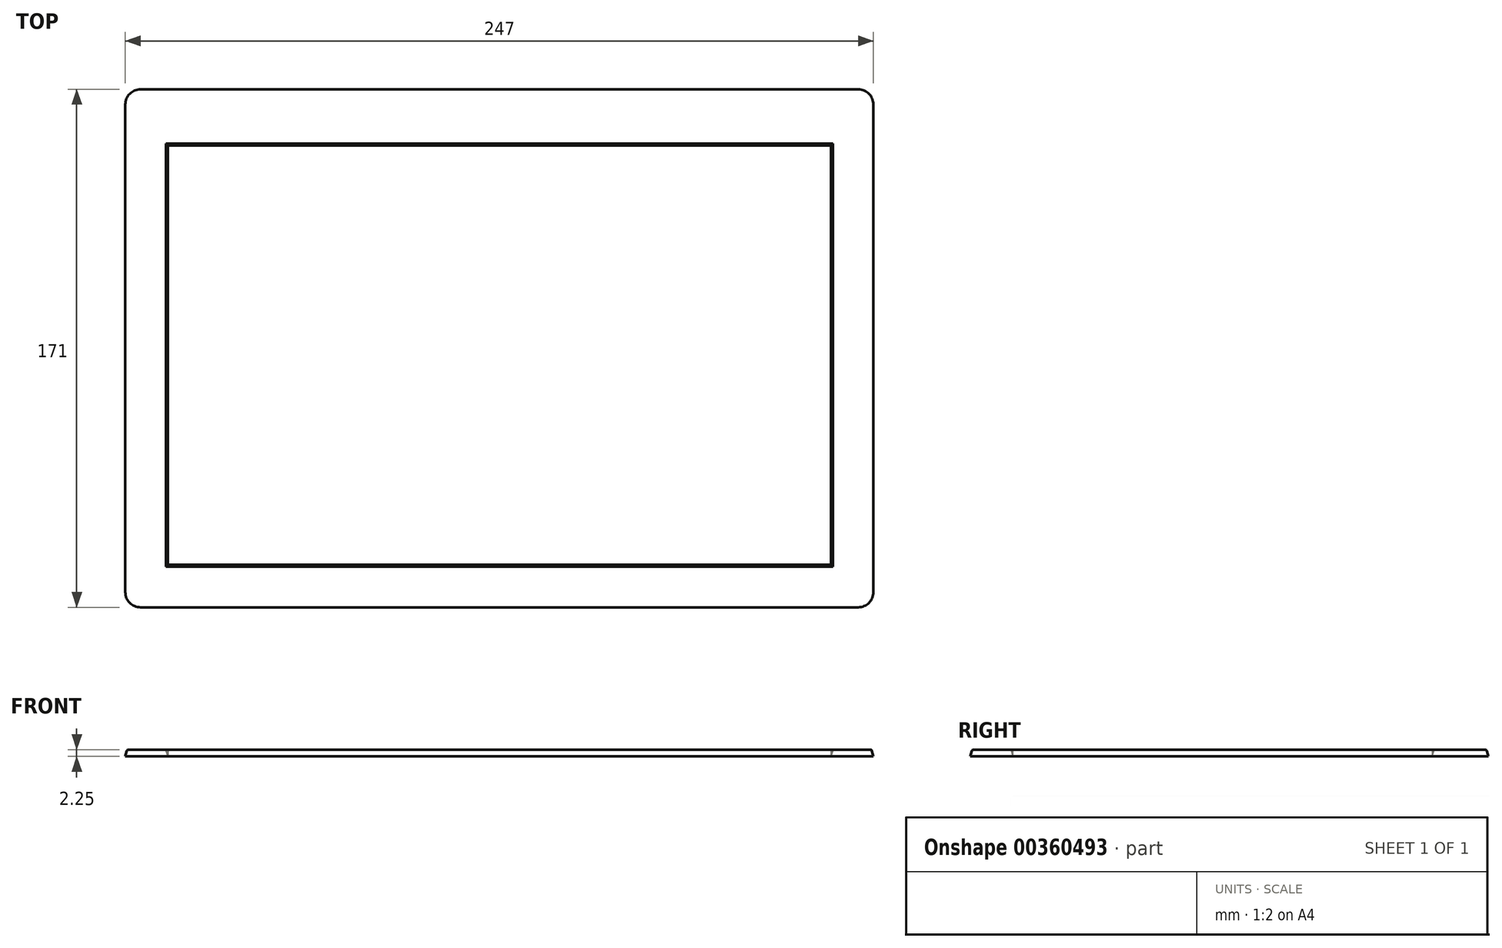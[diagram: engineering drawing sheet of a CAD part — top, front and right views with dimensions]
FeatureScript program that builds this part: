
annotation { "Feature Type Name" : "Feature", "Feature Type Description" : "" }
export const myFeature = defineFeature(function(context is Context, id is Id, definition is map)
    precondition{}
    {
        {
            var Q0;
            Q0=qCreatedBy(makeId("Top.planeOp"),FACE);
            var sketch = newSketch(context, id + "F0", { "sketchPlane" : qUnion([Q0])});
            skLineSegment(sketch, "E0.bottom", {"start": v(118.5, -85.5) * mm, "end": v(-118.5, -85.5) * mm});
            skLineSegment(sketch, "E0.top", {"start": v(118.5, 85.5) * mm, "end": v(-118.5, 85.5) * mm});
            skLineSegment(sketch, "E0.left", {"start": v(123.5, -80.5) * mm, "end": v(123.5, 80.5) * mm});
            skLineSegment(sketch, "E0.right", {"start": v(-123.5, -80.5) * mm, "end": v(-123.5, 80.5) * mm});
            skPoint(sketch, "E0.middle", {"position": v(0, 0) * mm});
            skLineSegment(sketch, "E1.bottom", {"start": v(-109.5, 67) * mm, "end": v(109.5, 67) * mm});
            skLineSegment(sketch, "E1.top", {"start": v(-109.5, -71.5) * mm, "end": v(109.5, -71.5) * mm});
            skLineSegment(sketch, "E1.left", {"start": v(-109.5, 67) * mm, "end": v(-109.5, -71.5) * mm});
            skLineSegment(sketch, "E1.right", {"start": v(109.5, 67) * mm, "end": v(109.5, -71.5) * mm});
            skPoint(sketch, "E2.visualSharp", {"position": v(-123.5, 85.5) * mm});
            skArc(sketch, "E2.filletArc", {"start": v(-118.5, 85.5) * mm, "mid": v(-122.04, 84.04) * mm, "end": v(-123.5, 80.5) * mm});
            skPoint(sketch, "E3.visualSharp", {"position": v(123.5, 85.5) * mm});
            skArc(sketch, "E3.filletArc", {"start": v(123.5, 80.5) * mm, "mid": v(122.04, 84.04) * mm, "end": v(118.5, 85.5) * mm});
            skPoint(sketch, "E4.visualSharp", {"position": v(123.5, -85.5) * mm});
            skArc(sketch, "E4.filletArc", {"start": v(118.5, -85.5) * mm, "mid": v(122.04, -84.04) * mm, "end": v(123.5, -80.5) * mm});
            skPoint(sketch, "E5.visualSharp", {"position": v(-123.5, -85.5) * mm});
            skArc(sketch, "E5.filletArc", {"start": v(-123.5, -80.5) * mm, "mid": v(-122.04, -84.04) * mm, "end": v(-118.5, -85.5) * mm});
            skSolve(sketch);
        }
        {
            var Q0;
            Q0=makeQuery(id+"F0.imprint","IMPRINT",FACE,{"disambiguationData":[TD([[makeQuery(id+"F0.imprint","IMPRINT",EDGE,{"derivedFrom":sQuery(id+"F0.wireOp",EDGE,"E0.bottom")}),-1.0]])]});
            extrude(context, id + "F1", {"entities" : qUnion([Q0]), "depth" : 2.25 * mm, "hasDraft" : true, "draftAngle" : 15 * degree, "draftPullDirection" : true});
        }
        {
            var Q0;
            Q0=makeQuery(id+"F0.imprint","IMPRINT",FACE,{"disambiguationData":[TD([[makeQuery(id+"F0.imprint","IMPRINT",EDGE,{"derivedFrom":sQuery(id+"F0.wireOp",EDGE,"E1.bottom")}),-1.0]])]});
            var Q1;
            Q1=makeQuery(id+"F1.opExtrude","CAP_FACE",FACE,{"disambiguationData":[OSD([sQuery(id+"F0.wireOp",EDGE,"E0.bottom"),sQuery(id+"F0.wireOp",EDGE,"E0.top"),sQuery(id+"F0.wireOp",EDGE,"E0.left"),sQuery(id+"F0.wireOp",EDGE,"E0.right"),sQuery(id+"F0.wireOp",EDGE,"E1.bottom"),sQuery(id+"F0.wireOp",EDGE,"E1.top"),sQuery(id+"F0.wireOp",EDGE,"E1.left"),sQuery(id+"F0.wireOp",EDGE,"E1.right")])],"isStart":false});
            extrude(context, id + "F2", {"entities" : qUnion([Q0]), "endBound" : BoundingType.UP_TO_SURFACE, "endBoundEntityFace" : qUnion([Q1]), "depth" : 25 * mm});
        }
        {
            var Q0;
            Q0=makeQuery(id+"F1.opExtrude","CAP_EDGE",EDGE,{"disambiguationData":[OSD([sQuery(id+"F0.wireOp",EDGE,"E0.right")])],"isStart":false});
            var Q1;
            Q1=makeQuery(id+"F1.opExtrude","CAP_EDGE",EDGE,{"disambiguationData":[OSD([sQuery(id+"F0.wireOp",EDGE,"E0.top")])],"isStart":false});
            var Q2;
            Q2=makeQuery(id+"F1.opExtrude","CAP_EDGE",EDGE,{"disambiguationData":[OSD([sQuery(id+"F0.wireOp",EDGE,"E0.bottom")])],"isStart":false});
            var Q3;
            Q3=makeQuery(id+"F1.opExtrude","CAP_EDGE",EDGE,{"disambiguationData":[OSD([sQuery(id+"F0.wireOp",EDGE,"E0.left")])],"isStart":false});
            fillet(context, id + "F3", {"entities" : qUnion([Q0, Q1, Q2, Q3]), "radius" : 0.5 * mm, "tangentPropagation" : true, "allowEdgeOverflow" : false});
        }
    });
